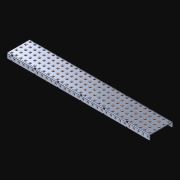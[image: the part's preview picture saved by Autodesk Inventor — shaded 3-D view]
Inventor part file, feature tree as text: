
AUTODESK INVENTOR PART (.ipt)
format: ipt  version: 2021 (Build 250183000, 183)  size: 2,370,560 bytes
history: native  units: in
note: dims shown in document units (in); Inventor stores cm internally (conversion verified against a paired STEP export)
features: extrude x218, other x218, sketch x4, pattern_linear x3
ambient origin geometry x8: Origin, YZ Plane, XZ Plane, XY Plane, X Axis, Y Axis, Z Axis, Center Point
bodies: Solid1 (feature_tree)
feature tree (443):
  pattern_linear  "Rectangular Pattern1"  Spacing1=0.182in  [1 undecoded]
  pattern_linear  "Rectangular Pattern2"  Spacing1=0.046in  [1 undecoded]
  pattern_linear  "Rectangular Pattern3"  Spacing1=0.5in  [1 undecoded]
  extrude  "Extrusion1"  Depth=0.046in
  sketch  "Sketch1"  dims[d0=0.182in]
  other  "Srf1"
  sketch  "Sketch2"  dims[d1=0.046in d2=0.0in]
  other  "Srf2"
  sketch  "Sketch3"  dims[d3=0.182in]
  other  "Srf3"
  other  "Srf4"
  other  "Srf5"
  other  "Srf6"
  other  "Srf7"
  other  "Srf8"
  other  "Srf9"
  other  "Srf10"
  other  "Srf11"
  other  "Srf12"
  other  "Srf13"
  other  "Srf14"
  other  "Srf15"
  other  "Srf16"
  other  "Srf17"
  other  "Srf18"
  other  "Srf19"
  other  "Srf20"
  other  "Srf21"
  other  "Srf22"
  other  "Srf23"
  other  "Srf24"
  other  "Srf25"
  other  "Srf26"
  other  "Srf27"
  other  "Srf28"
  other  "Srf29"
  other  "Srf30"
  other  "Srf31"
  other  "Srf32"
  other  "Srf33"
  other  "Srf38"
  other  "Srf39"
  other  "Srf40"
  other  "Srf41"
  other  "Srf42"
  other  "Srf43"
  other  "Srf44"
  other  "Srf45"
  other  "Srf46"
  other  "Srf47"
  other  "Srf48"
  other  "Srf49"
  other  "Srf50"
  other  "Srf51"
  other  "Srf52"
  other  "Srf53"
  other  "Srf54"
  other  "Srf55"
  other  "Srf56"
  other  "Srf57"
  other  "Srf58"
  other  "Srf59"
  other  "Srf60"
  other  "Srf61"
  other  "Srf62"
  other  "Srf63"
  other  "Srf64"
  other  "Srf65"
  other  "Srf66"
  other  "Srf67"
  other  "Srf72"
  other  "Srf73"
  other  "Srf74"
  other  "Srf75"
  other  "Srf76"
  other  "Srf77"
  other  "Srf78"
  other  "Srf79"
  other  "Srf80"
  other  "Srf81"
  other  "Srf82"
  other  "Srf83"
  other  "Srf84"
  other  "Srf85"
  other  "Srf86"
  other  "Srf87"
  other  "Srf88"
  other  "Srf89"
  other  "Srf90"
  other  "Srf91"
  other  "Srf92"
  other  "Srf93"
  other  "Srf94"
  other  "Srf95"
  other  "Srf96"
  other  "Srf97"
  other  "Srf98"
  other  "Srf99"
  other  "Srf100"
  other  "Srf101"
  other  "Srf102"
  other  "Srf107"
  other  "Srf108"
  other  "Srf109"
  other  "Srf110"
  other  "Srf111"
  other  "Srf112"
  other  "Srf113"
  other  "Srf114"
  other  "Srf115"
  other  "Srf116"
  other  "Srf117"
  other  "Srf118"
  other  "Srf119"
  other  "Srf120"
  other  "Srf121"
  other  "Srf122"
  other  "Srf123"
  other  "Srf124"
  other  "Srf125"
  other  "Srf126"
  other  "Srf127"
  other  "Srf128"
  other  "Srf129"
  other  "Srf130"
  other  "Srf131"
  other  "Srf132"
  other  "Srf133"
  other  "Srf134"
  other  "Srf135"
  other  "Srf136"
  other  "Srf137"
  other  "Srf142"
  other  "Srf143"
  other  "Srf144"
  other  "Srf145"
  other  "Srf146"
  other  "Srf147"
  other  "Srf148"
  other  "Srf149"
  other  "Srf150"
  other  "Srf151"
  other  "Srf152"
  other  "Srf153"
  other  "Srf154"
  other  "Srf155"
  other  "Srf156"
  other  "Srf157"
  other  "Srf158"
  other  "Srf159"
  other  "Srf160"
  other  "Srf161"
  other  "Srf162"
  other  "Srf163"
  other  "Srf164"
  other  "Srf165"
  other  "Srf166"
  other  "Srf167"
  other  "Srf168"
  other  "Srf169"
  other  "Srf170"
  other  "Srf171"
  other  "Srf172"
  other  "Srf177"
  other  "Srf178"
  other  "Srf179"
  other  "Srf180"
  other  "Srf181"
  other  "Srf182"
  other  "Srf183"
  other  "Srf184"
  other  "Srf185"
  other  "Srf186"
  other  "Srf187"
  other  "Srf188"
  other  "Srf189"
  other  "Srf190"
  other  "Srf191"
  other  "Srf192"
  other  "Srf193"
  other  "Srf194"
  other  "Srf195"
  other  "Srf196"
  other  "Srf197"
  other  "Srf198"
  other  "Srf199"
  other  "Srf200"
  other  "Srf201"
  other  "Srf202"
  other  "Srf203"
  other  "Srf204"
  other  "Srf205"
  other  "Srf206"
  other  "Srf207"
  other  "Srf212"
  other  "Srf213"
  other  "Srf214"
  other  "Srf215"
  other  "Srf216"
  other  "Srf217"
  other  "Srf218"
  other  "Srf219"
  other  "Srf220"
  other  "Srf221"
  other  "Srf222"
  other  "Srf223"
  other  "Srf224"
  other  "Srf225"
  other  "Srf226"
  other  "Srf227"
  other  "Srf228"
  other  "Srf229"
  other  "Srf230"
  other  "Srf231"
  other  "Srf232"
  other  "Srf233"
  other  "Srf234"
  other  "Srf235"
  other  "Srf236"
  other  "Srf237"
  other  "Srf238"
  other  "Srf239"
  other  "Srf240"
  other  "Srf241"
  sketch  "Sketch4"  dims[d4=0.046in d5=0.0in d6=0.182in d7=0.046in d8=0.0in d11=0.5in d12=12.2047in d14=0.5in d15=1.9685in d17=0.5in d18=12.2047in d20=0.5in d21=2.0in d22=0.0in]
  parser-record x1  (decoder bookkeeping rows leaked as tree rows — omitted from the tree; the rows remain in map.json)
  extrude  "ExtrusionSrf1"  Depth=0.046in
  extrude  "ExtrusionSrf2"  Depth=0.046in
  extrude  "ExtrusionSrf3"  Depth=0.046in
  extrude  "ExtrusionSrf4"  Depth=0.046in
  extrude  "ExtrusionSrf5"  Depth=0.046in
  extrude  "ExtrusionSrf6"  TaperAngle=0.0deg  [1 undecoded]
  extrude  "ExtrusionSrf7"  [1 undecoded]
  extrude  "ExtrusionSrf8"  [1 undecoded]
  extrude  "ExtrusionSrf9"  [1 undecoded]
  extrude  "ExtrusionSrf10"  [1 undecoded]
  extrude  "ExtrusionSrf11"  [1 undecoded]
  extrude  "ExtrusionSrf12"  [1 undecoded]
  extrude  "ExtrusionSrf13"  [1 undecoded]
  extrude  "ExtrusionSrf14"  [1 undecoded]
  extrude  "ExtrusionSrf15"  [1 undecoded]
  extrude  "ExtrusionSrf16"  [1 undecoded]
  extrude  "ExtrusionSrf17"  [1 undecoded]
  extrude  "ExtrusionSrf18"  [1 undecoded]
  extrude  "ExtrusionSrf19"  [1 undecoded]
  extrude  "ExtrusionSrf20"  [1 undecoded]
  extrude  "ExtrusionSrf21"  [1 undecoded]
  extrude  "ExtrusionSrf22"  [1 undecoded]
  extrude  "ExtrusionSrf23"  [1 undecoded]
  extrude  "ExtrusionSrf24"  [1 undecoded]
  extrude  "ExtrusionSrf25"  [1 undecoded]
  extrude  "ExtrusionSrf26"  [1 undecoded]
  extrude  "ExtrusionSrf27"  [1 undecoded]
  extrude  "ExtrusionSrf28"  [1 undecoded]
  extrude  "ExtrusionSrf29"  [1 undecoded]
  extrude  "ExtrusionSrf30"  [1 undecoded]
  extrude  "ExtrusionSrf31"  [1 undecoded]
  extrude  "ExtrusionSrf32"  [1 undecoded]
  extrude  "ExtrusionSrf33"  [1 undecoded]
  extrude  "ExtrusionSrf38"  [1 undecoded]
  extrude  "ExtrusionSrf39"  [1 undecoded]
  extrude  "ExtrusionSrf40"  [1 undecoded]
  extrude  "ExtrusionSrf41"  [1 undecoded]
  extrude  "ExtrusionSrf42"  [1 undecoded]
  extrude  "ExtrusionSrf43"  [1 undecoded]
  extrude  "ExtrusionSrf44"  [1 undecoded]
  extrude  "ExtrusionSrf45"  [1 undecoded]
  extrude  "ExtrusionSrf46"  [1 undecoded]
  extrude  "ExtrusionSrf47"  [1 undecoded]
  extrude  "ExtrusionSrf48"  [1 undecoded]
  extrude  "ExtrusionSrf49"  [1 undecoded]
  extrude  "ExtrusionSrf50"  [1 undecoded]
  extrude  "ExtrusionSrf51"  [1 undecoded]
  extrude  "ExtrusionSrf52"  [1 undecoded]
  extrude  "ExtrusionSrf53"  [1 undecoded]
  extrude  "ExtrusionSrf54"  [1 undecoded]
  extrude  "ExtrusionSrf55"  [1 undecoded]
  extrude  "ExtrusionSrf56"  [1 undecoded]
  extrude  "ExtrusionSrf57"  [1 undecoded]
  extrude  "ExtrusionSrf58"  [1 undecoded]
  extrude  "ExtrusionSrf59"  [1 undecoded]
  extrude  "ExtrusionSrf60"  [1 undecoded]
  extrude  "ExtrusionSrf61"  [1 undecoded]
  extrude  "ExtrusionSrf62"  [1 undecoded]
  extrude  "ExtrusionSrf63"  [1 undecoded]
  extrude  "ExtrusionSrf64"  [1 undecoded]
  extrude  "ExtrusionSrf65"  [1 undecoded]
  extrude  "ExtrusionSrf66"  [1 undecoded]
  extrude  "ExtrusionSrf67"  [1 undecoded]
  extrude  "ExtrusionSrf72"  [1 undecoded]
  extrude  "ExtrusionSrf73"  [1 undecoded]
  extrude  "ExtrusionSrf74"  [1 undecoded]
  extrude  "ExtrusionSrf75"  [1 undecoded]
  extrude  "ExtrusionSrf76"  [1 undecoded]
  extrude  "ExtrusionSrf77"  [1 undecoded]
  extrude  "ExtrusionSrf78"  [1 undecoded]
  extrude  "ExtrusionSrf79"  [1 undecoded]
  extrude  "ExtrusionSrf80"  [1 undecoded]
  extrude  "ExtrusionSrf81"  [1 undecoded]
  extrude  "ExtrusionSrf82"  [1 undecoded]
  extrude  "ExtrusionSrf83"  [1 undecoded]
  extrude  "ExtrusionSrf84"  [1 undecoded]
  extrude  "ExtrusionSrf85"  [1 undecoded]
  extrude  "ExtrusionSrf86"  [1 undecoded]
  extrude  "ExtrusionSrf87"  [1 undecoded]
  extrude  "ExtrusionSrf88"  [1 undecoded]
  extrude  "ExtrusionSrf89"  [1 undecoded]
  extrude  "ExtrusionSrf90"  [1 undecoded]
  extrude  "ExtrusionSrf91"  [1 undecoded]
  extrude  "ExtrusionSrf92"  [1 undecoded]
  extrude  "ExtrusionSrf93"  [1 undecoded]
  extrude  "ExtrusionSrf94"  [1 undecoded]
  extrude  "ExtrusionSrf95"  [1 undecoded]
  extrude  "ExtrusionSrf96"  [1 undecoded]
  extrude  "ExtrusionSrf97"  [1 undecoded]
  extrude  "ExtrusionSrf98"  [1 undecoded]
  extrude  "ExtrusionSrf99"  [1 undecoded]
  extrude  "ExtrusionSrf100"  [1 undecoded]
  extrude  "ExtrusionSrf101"  [1 undecoded]
  extrude  "ExtrusionSrf102"  [1 undecoded]
  extrude  "ExtrusionSrf107"  [1 undecoded]
  extrude  "ExtrusionSrf108"  [1 undecoded]
  extrude  "ExtrusionSrf109"  [1 undecoded]
  extrude  "ExtrusionSrf110"  [1 undecoded]
  extrude  "ExtrusionSrf111"  [1 undecoded]
  extrude  "ExtrusionSrf112"  [1 undecoded]
  extrude  "ExtrusionSrf113"  [1 undecoded]
  extrude  "ExtrusionSrf114"  [1 undecoded]
  extrude  "ExtrusionSrf115"  [1 undecoded]
  extrude  "ExtrusionSrf116"  [1 undecoded]
  extrude  "ExtrusionSrf117"  [1 undecoded]
  extrude  "ExtrusionSrf118"  [1 undecoded]
  extrude  "ExtrusionSrf119"  [1 undecoded]
  extrude  "ExtrusionSrf120"  [1 undecoded]
  extrude  "ExtrusionSrf121"  [1 undecoded]
  extrude  "ExtrusionSrf122"  [1 undecoded]
  extrude  "ExtrusionSrf123"  [1 undecoded]
  extrude  "ExtrusionSrf124"  [1 undecoded]
  extrude  "ExtrusionSrf125"  [1 undecoded]
  extrude  "ExtrusionSrf126"  [1 undecoded]
  extrude  "ExtrusionSrf127"  [1 undecoded]
  extrude  "ExtrusionSrf128"  [1 undecoded]
  extrude  "ExtrusionSrf129"  [1 undecoded]
  extrude  "ExtrusionSrf130"  [1 undecoded]
  extrude  "ExtrusionSrf131"  [1 undecoded]
  extrude  "ExtrusionSrf132"  [1 undecoded]
  extrude  "ExtrusionSrf133"  [1 undecoded]
  extrude  "ExtrusionSrf134"  [1 undecoded]
  extrude  "ExtrusionSrf135"  [1 undecoded]
  extrude  "ExtrusionSrf136"  [1 undecoded]
  extrude  "ExtrusionSrf137"  [1 undecoded]
  extrude  "ExtrusionSrf142"  [1 undecoded]
  extrude  "ExtrusionSrf143"  [1 undecoded]
  extrude  "ExtrusionSrf144"  [1 undecoded]
  extrude  "ExtrusionSrf145"  [1 undecoded]
  extrude  "ExtrusionSrf146"  [1 undecoded]
  extrude  "ExtrusionSrf147"  [1 undecoded]
  extrude  "ExtrusionSrf148"  [1 undecoded]
  extrude  "ExtrusionSrf149"  [1 undecoded]
  extrude  "ExtrusionSrf150"  [1 undecoded]
  extrude  "ExtrusionSrf151"  [1 undecoded]
  extrude  "ExtrusionSrf152"  [1 undecoded]
  extrude  "ExtrusionSrf153"  [1 undecoded]
  extrude  "ExtrusionSrf154"  [1 undecoded]
  extrude  "ExtrusionSrf155"  [1 undecoded]
  extrude  "ExtrusionSrf156"  [1 undecoded]
  extrude  "ExtrusionSrf157"  [1 undecoded]
  extrude  "ExtrusionSrf158"  [1 undecoded]
  extrude  "ExtrusionSrf159"  [1 undecoded]
  extrude  "ExtrusionSrf160"  [1 undecoded]
  extrude  "ExtrusionSrf161"  [1 undecoded]
  extrude  "ExtrusionSrf162"  [1 undecoded]
  extrude  "ExtrusionSrf163"  [1 undecoded]
  extrude  "ExtrusionSrf164"  [1 undecoded]
  extrude  "ExtrusionSrf165"  [1 undecoded]
  extrude  "ExtrusionSrf166"  [1 undecoded]
  extrude  "ExtrusionSrf167"  [1 undecoded]
  extrude  "ExtrusionSrf168"  [1 undecoded]
  extrude  "ExtrusionSrf169"  [1 undecoded]
  extrude  "ExtrusionSrf170"  [1 undecoded]
  extrude  "ExtrusionSrf171"  [1 undecoded]
  extrude  "ExtrusionSrf172"  [1 undecoded]
  extrude  "ExtrusionSrf177"  [1 undecoded]
  extrude  "ExtrusionSrf178"  [1 undecoded]
  extrude  "ExtrusionSrf179"  [1 undecoded]
  extrude  "ExtrusionSrf180"  [1 undecoded]
  extrude  "ExtrusionSrf181"  [1 undecoded]
  extrude  "ExtrusionSrf182"  [1 undecoded]
  extrude  "ExtrusionSrf183"  [1 undecoded]
  extrude  "ExtrusionSrf184"  [1 undecoded]
  extrude  "ExtrusionSrf185"  [1 undecoded]
  extrude  "ExtrusionSrf186"  [1 undecoded]
  extrude  "ExtrusionSrf187"  [1 undecoded]
  extrude  "ExtrusionSrf188"  [1 undecoded]
  extrude  "ExtrusionSrf189"  [1 undecoded]
  extrude  "ExtrusionSrf190"  [1 undecoded]
  extrude  "ExtrusionSrf191"  [1 undecoded]
  extrude  "ExtrusionSrf192"  [1 undecoded]
  extrude  "ExtrusionSrf193"  [1 undecoded]
  extrude  "ExtrusionSrf194"  [1 undecoded]
  extrude  "ExtrusionSrf195"  [1 undecoded]
  extrude  "ExtrusionSrf196"  [1 undecoded]
  extrude  "ExtrusionSrf197"  [1 undecoded]
  extrude  "ExtrusionSrf198"  [1 undecoded]
  extrude  "ExtrusionSrf199"  [1 undecoded]
  extrude  "ExtrusionSrf200"  [1 undecoded]
  extrude  "ExtrusionSrf201"  [1 undecoded]
  extrude  "ExtrusionSrf202"  [1 undecoded]
  extrude  "ExtrusionSrf203"  [1 undecoded]
  extrude  "ExtrusionSrf204"  [1 undecoded]
  extrude  "ExtrusionSrf205"  [1 undecoded]
  extrude  "ExtrusionSrf206"  [1 undecoded]
  extrude  "ExtrusionSrf207"  [1 undecoded]
  extrude  "ExtrusionSrf212"  [1 undecoded]
  extrude  "ExtrusionSrf213"  [1 undecoded]
  extrude  "ExtrusionSrf214"  [1 undecoded]
  extrude  "ExtrusionSrf215"  [1 undecoded]
  extrude  "ExtrusionSrf216"  [1 undecoded]
  extrude  "ExtrusionSrf217"  [1 undecoded]
  extrude  "ExtrusionSrf218"  [1 undecoded]
  extrude  "ExtrusionSrf219"  [1 undecoded]
  extrude  "ExtrusionSrf220"  [1 undecoded]
  extrude  "ExtrusionSrf221"  [1 undecoded]
  extrude  "ExtrusionSrf222"  [1 undecoded]
  extrude  "ExtrusionSrf223"  [1 undecoded]
  extrude  "ExtrusionSrf224"  [1 undecoded]
  extrude  "ExtrusionSrf225"  [1 undecoded]
  extrude  "ExtrusionSrf226"  [1 undecoded]
  extrude  "ExtrusionSrf227"  [1 undecoded]
  extrude  "ExtrusionSrf228"  [1 undecoded]
  extrude  "ExtrusionSrf229"  [1 undecoded]
  extrude  "ExtrusionSrf230"  [1 undecoded]
  extrude  "ExtrusionSrf231"  [1 undecoded]
  extrude  "ExtrusionSrf232"  [1 undecoded]
  extrude  "ExtrusionSrf233"  [1 undecoded]
  extrude  "ExtrusionSrf234"  [1 undecoded]
  extrude  "ExtrusionSrf235"  [1 undecoded]
  extrude  "ExtrusionSrf236"  [1 undecoded]
  extrude  "ExtrusionSrf237"  [1 undecoded]
  extrude  "ExtrusionSrf238"  [1 undecoded]
  extrude  "ExtrusionSrf239"  [1 undecoded]
  extrude  "ExtrusionSrf240"  [1 undecoded]
  extrude  "ExtrusionSrf241"  [1 undecoded]
note: 215 required parameter values undecoded (feature->parameter linkage not recoverable at this tier; creation-order binding heuristic only, values carry confidence <= 0.55)
